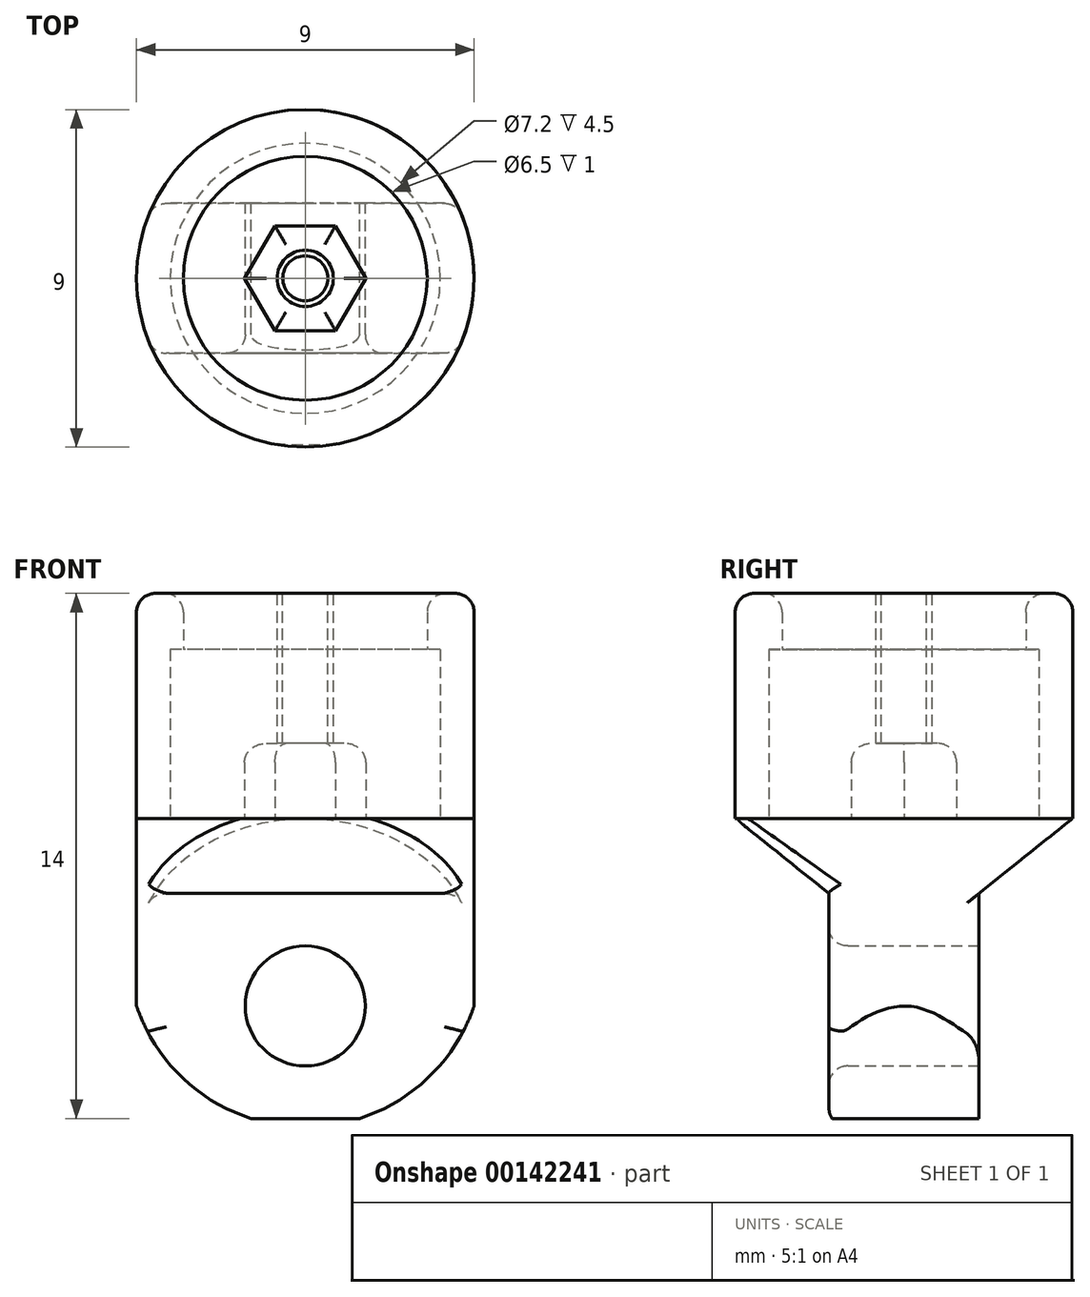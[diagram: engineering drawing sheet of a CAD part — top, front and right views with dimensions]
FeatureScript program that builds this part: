
annotation { "Feature Type Name" : "Feature", "Feature Type Description" : "" }
export const myFeature = defineFeature(function(context is Context, id is Id, definition is map)
    precondition{}
    {
        {
            var Q0;
            Q0=qCreatedBy(makeId("Top.planeOp"),FACE);
            var sketch = newSketch(context, id + "F0", { "sketchPlane" : qUnion([Q0])});
            skCircle(sketch, "E0", {"center": v(0, 0) * mm, "radius": 3.6 * mm});
            skCircle(sketch, "E1", {"center": v(0, 0) * mm, "radius": 4.5 * mm});
            skCircle(sketch, "E2.cCircle", {"center": v(0, 0) * mm, "radius": 1.4 * mm, "construction": true});
            skLineSegment(sketch, "E2.0", {"start": v(0.8, -1.4) * mm, "end": v(-0.8, -1.4) * mm});
            skLineSegment(sketch, "E2.1", {"start": v(-0.8, -1.4) * mm, "end": v(-1.62, 0) * mm});
            skLineSegment(sketch, "E2.2", {"start": v(-1.62, 0) * mm, "end": v(-0.8, 1.4) * mm});
            skLineSegment(sketch, "E2.3", {"start": v(-0.8, 1.4) * mm, "end": v(0.8, 1.4) * mm});
            skLineSegment(sketch, "E2.4", {"start": v(0.8, 1.4) * mm, "end": v(1.62, 0) * mm});
            skLineSegment(sketch, "E2.5", {"start": v(1.62, 0) * mm, "end": v(0.8, -1.4) * mm});
            skPoint(sketch, "E2.0.midPoint", {"position": v(0, -1.4) * mm});
            skSolve(sketch);
        }
        {
            var Q0;
            Q0 = qSketchRegion(id + "F0", true);
            var Q1;
            Q1=makeQuery(id+"F0.imprint","IMPRINT",FACE,{"disambiguationData":[TD([[makeQuery(id+"F0.imprint","IMPRINT",EDGE,{"derivedFrom":sQuery(id+"F0.wireOp",EDGE,"E0")}),-1.0]])]});
            extrude(context, id + "F1", {"entities" : qUnion([Q0, Q1]), "depth" : 4.5 * mm});
        }
        {
            var Q0;
            Q0=qCreatedBy(makeId("Top.planeOp"),FACE);
            var sketch = newSketch(context, id + "F2", { "sketchPlane" : qUnion([Q0])});
            skCircle(sketch, "E3", {"center": v(0, 0) * mm, "radius": 3.5 * mm});
            skCircle(sketch, "E4", {"center": v(0, 0) * mm, "radius": 4.5 * mm});
            skSolve(sketch);
        }
        {
            var Q0;
            Q0=makeQuery(id+"F1.opExtrude","CAP_FACE",FACE,{"disambiguationData":[OSD([sQuery(id+"F0.wireOp",EDGE,"E0"),sQuery(id+"F0.wireOp",EDGE,"E1")])],"isStart":false});
            var sketch = newSketch(context, id + "F3", { "sketchPlane" : qUnion([Q0])});
            skCircle(sketch, "E5", {"center": v(0, 0) * mm, "radius": 3.25 * mm});
            skCircle(sketch, "E6.0", {"center": v(0, 0) * mm, "radius": 4.5 * mm});
            skCircle(sketch, "E7", {"center": v(0, 0) * mm, "radius": 0.5 * mm});
            skCircle(sketch, "E8", {"center": v(0, 0) * mm, "radius": 0.25 * mm});
            skSolve(sketch);
        }
        {
            var Q0;
            Q0 = qSketchRegion(id + "F3", true);
            extrude(context, id + "F4", {"entities" : qUnion([Q0]), "operationType" : NewBodyOperationType.ADD, "depth" : 1.5 * mm});
        }
        {
            var Q0;
            Q0=makeQuery(id+"F0.imprint","IMPRINT",FACE,{"disambiguationData":[TD([[makeQuery(id+"F0.imprint","IMPRINT",EDGE,{"derivedFrom":sQuery(id+"F0.wireOp",EDGE,"E2.0")}),-1.0]])]});
            extrude(context, id + "F5", {"entities" : qUnion([Q0]), "depth" : 2 * mm});
        }
        {
            var Q0;
            Q0=makeQuery(id+"F0.imprint","IMPRINT",FACE,{"disambiguationData":[TD([[makeQuery(id+"F0.imprint","IMPRINT",EDGE,{"derivedFrom":sQuery(id+"F0.wireOp",EDGE,"E0")}),-1.0]])]});
            var Q1;
            Q1=makeQuery(id+"F0.imprint","IMPRINT",FACE,{"disambiguationData":[TD([[makeQuery(id+"F0.imprint","IMPRINT",EDGE,{"derivedFrom":sQuery(id+"F0.wireOp",EDGE,"E0")}),1.0]])]});
            var Q2;
            Q2=makeQuery(id+"F0.imprint","IMPRINT",FACE,{"disambiguationData":[TD([[makeQuery(id+"F0.imprint","IMPRINT",EDGE,{"derivedFrom":sQuery(id+"F0.wireOp",EDGE,"E2.0")}),-1.0]])]});
            extrude(context, id + "F6", {"entities" : qUnion([Q0, Q1, Q2]), "oppositeDirection" : true, "depth" : 8 * mm});
        }
        {
            var Q0;
            Q0=qCreatedBy(makeId("Right.planeOp"),FACE);
            var sketch = newSketch(context, id + "F7", { "sketchPlane" : qUnion([Q0])});
            skLineSegment(sketch, "E9", {"start": v(2, -8) * mm, "end": v(2, -2) * mm});
            skLineSegment(sketch, "E10", {"start": v(2, -2) * mm, "end": v(4.5, 0) * mm});
            skLineSegment(sketch, "E11.MirrorCS", {"start": v(-2, -2) * mm, "end": v(-4.5, 0) * mm});
            skLineSegment(sketch, "E12.MirrorCS", {"start": v(-2, -8) * mm, "end": v(-2, -2) * mm});
            skLineSegment(sketch, "E13", {"start": v(-4.5, -8) * mm, "end": v(-4.5, 0) * mm});
            skLineSegment(sketch, "E14", {"start": v(-2, -8) * mm, "end": v(-4.5, -8) * mm});
            skLineSegment(sketch, "E15", {"start": v(2, -8) * mm, "end": v(4.5, -8) * mm});
            skLineSegment(sketch, "E16", {"start": v(-4.5, 0) * mm, "end": v(-4.5, -8) * mm});
            skLineSegment(sketch, "E17", {"start": v(4.5, 0) * mm, "end": v(2, -2) * mm});
            skLineSegment(sketch, "E18", {"start": v(4.5, 0) * mm, "end": v(4.5, -8) * mm});
            skSolve(sketch);
        }
        {
            var Q0;
            Q0 = qSketchRegion(id + "F7", true);
            extrude(context, id + "F8", {"entities" : qUnion([Q0]), "operationType" : NewBodyOperationType.REMOVE, "endBound" : BoundingType.THROUGH_ALL, "oppositeDirection" : true, "depth" : 25 * mm, "hasSecondDirection" : true, "secondDirectionBound" : SecondDirectionBoundingType.THROUGH_ALL, "secondDirectionOppositeDirection" : false, "secondDirectionDepth" : 25 * mm});
        }
        {
            var Q0;
            Q0=makeQuery(id+"F8.boolean.opBoolean","COPY",FACE,{"derivedFrom":makeQuery(id+"F8.opExtrude","SWEPT_FACE",FACE,{"disambiguationData":[OSD([sQuery(id+"F7.wireOp",EDGE,"E9")])]})});
            var sketch = newSketch(context, id + "F9", { "sketchPlane" : qUnion([Q0])});
            skCircle(sketch, "E19", {"center": v(0, -5) * mm, "radius": 1.6 * mm});
            skLineSegment(sketch, "E20", {"start": v(-4.5, -8) * mm, "end": v(-4.5, 0) * mm});
            skLineSegment(sketch, "E21", {"start": v(4.5, 0) * mm, "end": v(4.5, -8) * mm});
            skLineSegment(sketch, "E22", {"start": v(0, -5) * mm, "end": v(-4.5, -5) * mm, "construction": true});
            skPoint(sketch, "E22.endSnap0", {"position": v(-4.03, -5) * mm});
            skLineSegment(sketch, "E23", {"start": v(0, -5) * mm, "end": v(4.5, -5) * mm, "construction": true});
            skArc(sketch, "E24", {"start": v(-4.5, -5) * mm, "mid": v(0, -8.23) * mm, "end": v(4.5, -5) * mm});
            skLineSegment(sketch, "E25.0", {"start": v(4.03, -8) * mm, "end": v(-4.03, -8) * mm});
            skLineSegment(sketch, "E26.0", {"start": v(-4.03, -8) * mm, "end": v(-4.5, -8) * mm});
            skLineSegment(sketch, "E27", {"start": v(4.03, -8) * mm, "end": v(4.5, -8) * mm});
            skSolve(sketch);
        }
        {
            var Q0;
            {var subQ5=sQuery(id+"F9.wireOp",EDGE,"E27");Q0=makeQuery(id+"F9.imprint","IMPRINT",FACE,{"disambiguationData":[TD([[makeQuery(id+"F9.imprint","IMPRINT",EDGE,{"derivedFrom":subQ5}),1.0]])]});}
            var Q1;
            {var subQ0=sQuery(id+"F9.wireOp",EDGE,"E25.0");var subQ1=sQuery(id+"F9.wireOp",EDGE,"E24");var subQ2=makeQuery(id+"F9.imprint","INTERSECT",VERTEX,{"disambiguationData":[OD(1.0)],"derivedFrom":[subQ1,subQ0]});Q1=makeQuery(id+"F9.imprint","IMPRINT",FACE,{"disambiguationData":[TD([[makeQuery(id+"F9.imprint","IMPRINT",EDGE,{"disambiguationData":[TD([[subQ2,-1.0]])],"derivedFrom":subQ1}),-1.0]])]});}
            var Q2;
            {var subQ0=sQuery(id+"F9.wireOp",EDGE,"E25.0");var subQ1=sQuery(id+"F9.wireOp",EDGE,"E24");var subQ2=makeQuery(id+"F9.imprint","INTERSECT",VERTEX,{"disambiguationData":[OD(0.0)],"derivedFrom":[subQ1,subQ0]});Q2=makeQuery(id+"F9.imprint","IMPRINT",FACE,{"disambiguationData":[TD([[makeQuery(id+"F9.imprint","IMPRINT",EDGE,{"disambiguationData":[TD([[subQ2,1.0]])],"derivedFrom":subQ1}),-1.0]])]});}
            var Q3;
            {var subQ0=sQuery(id+"F9.wireOp",EDGE,"E26.0");Q3=makeQuery(id+"F9.imprint","IMPRINT",FACE,{"disambiguationData":[TD([[makeQuery(id+"F9.imprint","IMPRINT",EDGE,{"derivedFrom":subQ0}),-1.0]])]});}
            var Q4;
            Q4=makeQuery(id+"F9.imprint","IMPRINT",FACE,{"disambiguationData":[TD([[makeQuery(id+"F9.imprint","IMPRINT",EDGE,{"derivedFrom":sQuery(id+"F9.wireOp",EDGE,"E19")}),1.0]])]});
            extrude(context, id + "F10", {"entities" : qUnion([Q0, Q1, Q2, Q3, Q4]), "operationType" : NewBodyOperationType.REMOVE, "oppositeDirection" : true, "depth" : 25 * mm});
        }
        {
            var Q0;
            Q0=makeQuery(id+"F4.opExtrude","CAP_EDGE",EDGE,{"disambiguationData":[OSD([sQuery(id+"F3.wireOp",EDGE,"E6.0")])],"isStart":false});
            var Q1;
            Q1=makeQuery(id+"F4.opExtrude","CAP_EDGE",EDGE,{"disambiguationData":[OSD([sQuery(id+"F3.wireOp",EDGE,"E5")])],"isStart":false});
            var Q2;
            Q2=makeQuery(id+"F5.opExtrude","CAP_EDGE",EDGE,{"disambiguationData":[OSD([sQuery(id+"F0.wireOp",EDGE,"E2.4")])],"isStart":false});
            var Q3;
            Q3=makeQuery(id+"F5.opExtrude","CAP_EDGE",EDGE,{"disambiguationData":[OSD([sQuery(id+"F0.wireOp",EDGE,"E2.3")])],"isStart":false});
            var Q4;
            Q4=makeQuery(id+"F5.opExtrude","CAP_EDGE",EDGE,{"disambiguationData":[OSD([sQuery(id+"F0.wireOp",EDGE,"E2.2")])],"isStart":false});
            var Q5;
            Q5=makeQuery(id+"F5.opExtrude","CAP_EDGE",EDGE,{"disambiguationData":[OSD([sQuery(id+"F0.wireOp",EDGE,"E2.1")])],"isStart":false});
            var Q6;
            Q6=makeQuery(id+"F5.opExtrude","CAP_EDGE",EDGE,{"disambiguationData":[OSD([sQuery(id+"F0.wireOp",EDGE,"E2.0")])],"isStart":false});
            var Q7;
            Q7=makeQuery(id+"F5.opExtrude","CAP_EDGE",EDGE,{"disambiguationData":[OSD([sQuery(id+"F0.wireOp",EDGE,"E2.5")])],"isStart":false});
            var Q8;
            {var subQ0=sQuery(id+"F9.wireOp",EDGE,"E24");Q8=makeQuery(id+"F10.boolean.opBoolean","COPY",EDGE,{"derivedFrom":makeQuery(id+"F10.opExtrude","CAP_EDGE",EDGE,{"disambiguationData":[OSD([subQ0]),TDD([makeQuery(id+"F9.imprint","IMPRINT",EDGE,{"disambiguationData":[TD([[makeQuery(id+"F9.imprint","INTERSECT",VERTEX,{"disambiguationData":[OD(1.0)],"derivedFrom":[subQ0,sQuery(id+"F9.wireOp",EDGE,"E25.0")]}),-1.0]])],"derivedFrom":subQ0}),makeQuery(id+"F9.imprint","IMPRINT",EDGE,{"disambiguationData":[TD([[makeQuery(id+"F9.imprint","INTERSECT",VERTEX,{"derivedFrom":[subQ0,sQuery(id+"F9.wireOp",EDGE,"E21")]}),1.0]])],"derivedFrom":subQ0})])],"isStart":true})});}
            var Q9;
            Q9=makeQuery(id+"F8.boolean.opBoolean","COPY",EDGE,{"derivedFrom":makeQuery(id+"F8.opExtrude","SWEPT_EDGE",EDGE,{"disambiguationData":[OSD([sQuery(id+"F7.wireOp",EDGE,"E9"),sQuery(id+"F7.wireOp",EDGE,"E15")])]})});
            var Q10;
            {var subQ0=sQuery(id+"F9.wireOp",EDGE,"E24");Q10=makeQuery(id+"F10.boolean.opBoolean","COPY",EDGE,{"derivedFrom":makeQuery(id+"F10.opExtrude","CAP_EDGE",EDGE,{"disambiguationData":[OSD([subQ0]),TDD([makeQuery(id+"F9.imprint","IMPRINT",EDGE,{"disambiguationData":[TD([[makeQuery(id+"F9.imprint","INTERSECT",VERTEX,{"derivedFrom":[sQuery(id+"F9.wireOp",EDGE,"E20"),subQ0]}),-1.0]])],"derivedFrom":subQ0}),makeQuery(id+"F9.imprint","IMPRINT",EDGE,{"disambiguationData":[TD([[makeQuery(id+"F9.imprint","INTERSECT",VERTEX,{"disambiguationData":[OD(0.0)],"derivedFrom":[subQ0,sQuery(id+"F9.wireOp",EDGE,"E25.0")]}),1.0]])],"derivedFrom":subQ0})])],"isStart":true})});}
            var Q11;
            Q11=makeQuery(id+"F8.boolean.opBoolean","INTERSECT",EDGE,{"disambiguationData":[OD(1.0)],"derivedFrom":[makeQuery(id+"F6.opExtrude","SWEPT_FACE",FACE,{"disambiguationData":[OSD([sQuery(id+"F0.wireOp",EDGE,"E1")])]}),makeQuery(id+"F8.opExtrude","SWEPT_FACE",FACE,{"disambiguationData":[OSD([sQuery(id+"F7.wireOp",EDGE,"E9")])]})]});
            var Q12;
            Q12=makeQuery(id+"F8.boolean.opBoolean","INTERSECT",EDGE,{"disambiguationData":[OD(0.0)],"derivedFrom":[makeQuery(id+"F6.opExtrude","SWEPT_FACE",FACE,{"disambiguationData":[OSD([sQuery(id+"F0.wireOp",EDGE,"E1")])]}),makeQuery(id+"F8.opExtrude","SWEPT_FACE",FACE,{"disambiguationData":[OSD([sQuery(id+"F7.wireOp",EDGE,"E9")])]})]});
            var Q13;
            Q13=makeQuery(id+"F8.boolean.opBoolean","COPY",EDGE,{"derivedFrom":makeQuery(id+"F8.opExtrude","SWEPT_EDGE",EDGE,{"disambiguationData":[OSD([sQuery(id+"F7.wireOp",EDGE,"E12.MirrorCS"),sQuery(id+"F7.wireOp",EDGE,"E14")])]})});
            var Q14;
            {var subQ0=sQuery(id+"F9.wireOp",EDGE,"E24");Q14=makeQuery(id+"F10.boolean.opBoolean","INTERSECT",EDGE,{"derivedFrom":[makeQuery(id+"F8.boolean.opBoolean","COPY",FACE,{"derivedFrom":makeQuery(id+"F8.opExtrude","SWEPT_FACE",FACE,{"disambiguationData":[OSD([sQuery(id+"F7.wireOp",EDGE,"E12.MirrorCS")])]})}),makeQuery(id+"F10.opExtrude","SWEPT_FACE",FACE,{"disambiguationData":[OSD([subQ0]),TDD([makeQuery(id+"F9.imprint","IMPRINT",EDGE,{"disambiguationData":[TD([[makeQuery(id+"F9.imprint","INTERSECT",VERTEX,{"derivedFrom":[sQuery(id+"F9.wireOp",EDGE,"E20"),subQ0]}),-1.0]])],"derivedFrom":subQ0}),makeQuery(id+"F9.imprint","IMPRINT",EDGE,{"disambiguationData":[TD([[makeQuery(id+"F9.imprint","INTERSECT",VERTEX,{"disambiguationData":[OD(0.0)],"derivedFrom":[subQ0,sQuery(id+"F9.wireOp",EDGE,"E25.0")]}),1.0]])],"derivedFrom":subQ0})])]})]});}
            var Q15;
            {var subQ0=sQuery(id+"F9.wireOp",EDGE,"E24");Q15=makeQuery(id+"F10.boolean.opBoolean","INTERSECT",EDGE,{"derivedFrom":[makeQuery(id+"F8.boolean.opBoolean","COPY",FACE,{"derivedFrom":makeQuery(id+"F8.opExtrude","SWEPT_FACE",FACE,{"disambiguationData":[OSD([sQuery(id+"F7.wireOp",EDGE,"E12.MirrorCS")])]})}),makeQuery(id+"F10.opExtrude","SWEPT_FACE",FACE,{"disambiguationData":[OSD([subQ0]),TDD([makeQuery(id+"F9.imprint","IMPRINT",EDGE,{"disambiguationData":[TD([[makeQuery(id+"F9.imprint","INTERSECT",VERTEX,{"disambiguationData":[OD(1.0)],"derivedFrom":[subQ0,sQuery(id+"F9.wireOp",EDGE,"E25.0")]}),-1.0]])],"derivedFrom":subQ0}),makeQuery(id+"F9.imprint","IMPRINT",EDGE,{"disambiguationData":[TD([[makeQuery(id+"F9.imprint","INTERSECT",VERTEX,{"derivedFrom":[subQ0,sQuery(id+"F9.wireOp",EDGE,"E21")]}),1.0]])],"derivedFrom":subQ0})])]})]});}
            var Q16;
            Q16=makeQuery(id+"F8.boolean.opBoolean","INTERSECT",EDGE,{"disambiguationData":[OD(0.0)],"derivedFrom":[makeQuery(id+"F6.opExtrude","SWEPT_FACE",FACE,{"disambiguationData":[OSD([sQuery(id+"F0.wireOp",EDGE,"E1")])]}),makeQuery(id+"F8.opExtrude","SWEPT_FACE",FACE,{"disambiguationData":[OSD([sQuery(id+"F7.wireOp",EDGE,"E12.MirrorCS")])]})]});
            var Q17;
            Q17=makeQuery(id+"F8.boolean.opBoolean","INTERSECT",EDGE,{"disambiguationData":[OD(1.0)],"derivedFrom":[makeQuery(id+"F6.opExtrude","SWEPT_FACE",FACE,{"disambiguationData":[OSD([sQuery(id+"F0.wireOp",EDGE,"E1")])]}),makeQuery(id+"F8.opExtrude","SWEPT_FACE",FACE,{"disambiguationData":[OSD([sQuery(id+"F7.wireOp",EDGE,"E12.MirrorCS")])]})]});
            var Q18;
            Q18=makeQuery(id+"F8.boolean.opBoolean","INTERSECT",EDGE,{"disambiguationData":[OD(1.0)],"derivedFrom":[makeQuery(id+"F6.opExtrude","SWEPT_FACE",FACE,{"disambiguationData":[OSD([sQuery(id+"F0.wireOp",EDGE,"E1")])]}),makeQuery(id+"F8.opExtrude","SWEPT_FACE",FACE,{"disambiguationData":[OSD([sQuery(id+"F7.wireOp",EDGE,"E11.MirrorCS")])]})]});
            var Q19;
            Q19=makeQuery(id+"F8.boolean.opBoolean","INTERSECT",EDGE,{"disambiguationData":[OD(0.0)],"derivedFrom":[makeQuery(id+"F6.opExtrude","SWEPT_FACE",FACE,{"disambiguationData":[OSD([sQuery(id+"F0.wireOp",EDGE,"E1")])]}),makeQuery(id+"F8.opExtrude","SWEPT_FACE",FACE,{"disambiguationData":[OSD([sQuery(id+"F7.wireOp",EDGE,"E17")])]})]});
            var Q20;
            Q20=makeQuery(id+"F10.boolean.opBoolean","COPY",EDGE,{"derivedFrom":makeQuery(id+"F10.opExtrude","CAP_EDGE",EDGE,{"disambiguationData":[OSD([sQuery(id+"F9.wireOp",EDGE,"E19")])],"isStart":true})});
            var Q21;
            Q21=makeQuery(id+"F10.boolean.opBoolean","INTERSECT",EDGE,{"derivedFrom":[makeQuery(id+"F8.boolean.opBoolean","COPY",FACE,{"derivedFrom":makeQuery(id+"F8.opExtrude","SWEPT_FACE",FACE,{"disambiguationData":[OSD([sQuery(id+"F7.wireOp",EDGE,"E12.MirrorCS")])]})}),makeQuery(id+"F10.opExtrude","SWEPT_FACE",FACE,{"disambiguationData":[OSD([sQuery(id+"F9.wireOp",EDGE,"E19")])]})]});
            fillet(context, id + "F11", {"entities" : qUnion([Q0, Q1, Q2, Q3, Q4, Q5, Q6, Q7, Q8, Q9, Q10, Q11, Q12, Q13, Q14, Q15, Q16, Q17, Q18, Q19, Q20, Q21]), "radius" : 0.5 * mm, "tangentPropagation" : true, "allowEdgeOverflow" : false});
        }
        {
            var Q0;
            Q0=makeQuery(id+"F4.opExtrude","CAP_FACE",FACE,{"disambiguationData":[OSD([sQuery(id+"F3.wireOp",EDGE,"E5"),sQuery(id+"F3.wireOp",EDGE,"E6.0")])],"isStart":false});
            var sketch = newSketch(context, id + "F12", { "sketchPlane" : qUnion([Q0])});
            skCircle(sketch, "E28", {"center": v(0, 0) * mm, "radius": 0.75 * mm});
            skCircle(sketch, "E29", {"center": v(0, 0) * mm, "radius": 0.6 * mm});
            skSolve(sketch);
        }
        {
            var Q0;
            Q0=makeQuery(id+"F12.imprint","IMPRINT",FACE,{"disambiguationData":[TD([[makeQuery(id+"F12.imprint","IMPRINT",EDGE,{"derivedFrom":sQuery(id+"F12.wireOp",EDGE,"E28")}),1.0]])]});
            extrude(context, id + "F13", {"entities" : qUnion([Q0]), "operationType" : NewBodyOperationType.ADD, "endBound" : BoundingType.UP_TO_NEXT, "oppositeDirection" : true, "depth" : 25 * mm});
        }
    });
